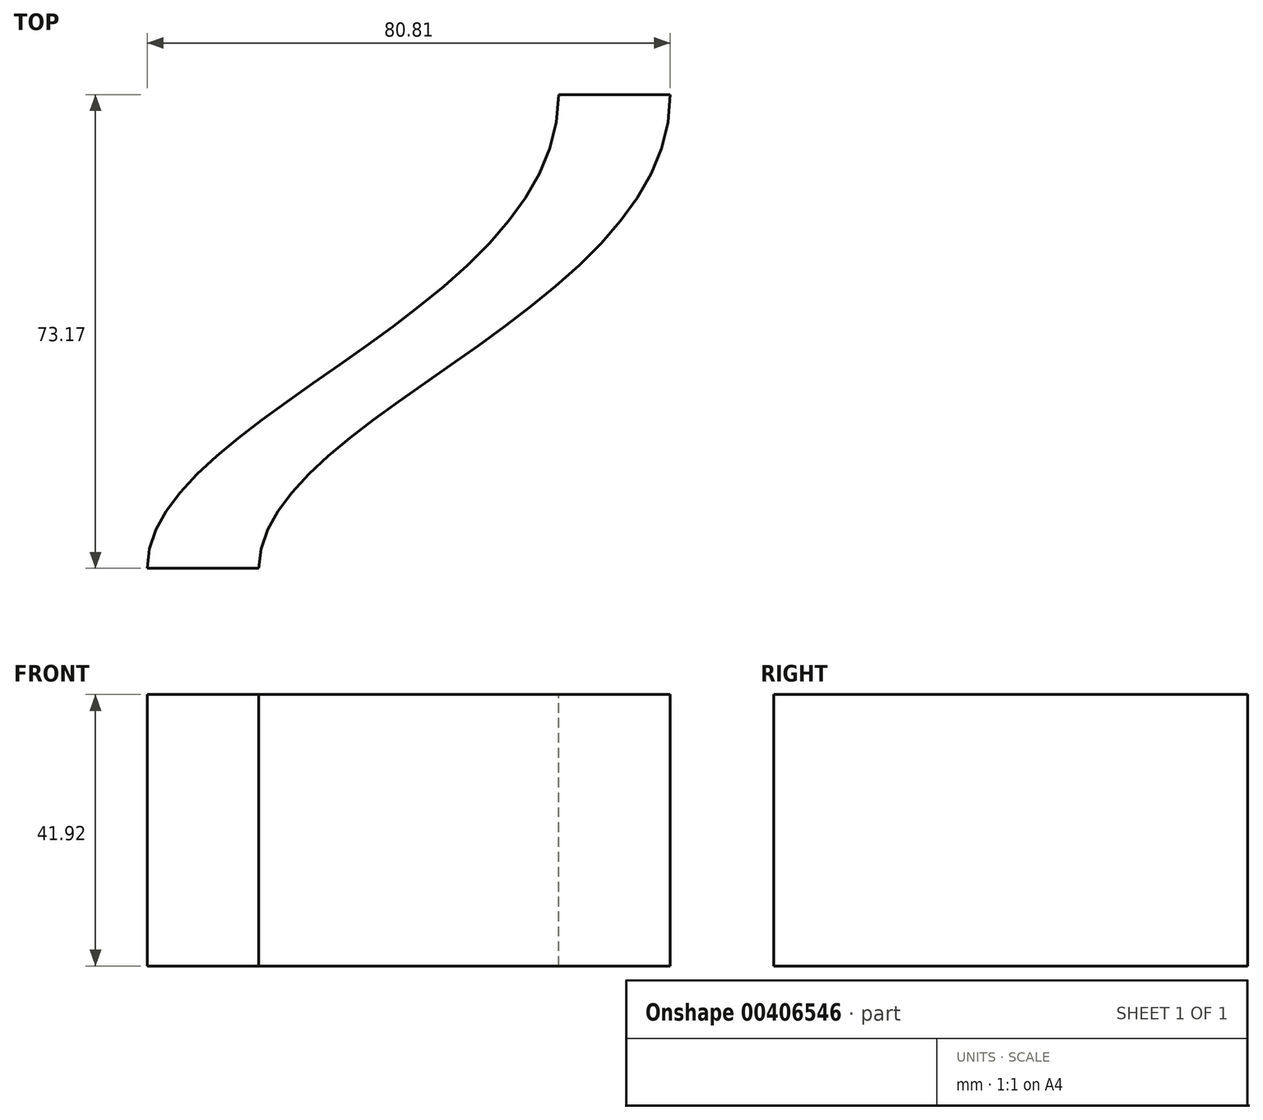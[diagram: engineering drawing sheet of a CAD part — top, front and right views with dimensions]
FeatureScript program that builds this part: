
annotation { "Feature Type Name" : "Feature", "Feature Type Description" : "" }
export const myFeature = defineFeature(function(context is Context, id is Id, definition is map)
    precondition{}
    {
        {
            var Q0;
            Q0=qCreatedBy(makeId("Front.planeOp"),FACE);
            var sketch = newSketch(context, id + "F0", { "sketchPlane" : qUnion([Q0])});
            skLineSegment(sketch, "E0", {"start": v(-49.03, 0) * mm, "end": v(-49.03, 41.92) * mm});
            skLineSegment(sketch, "E1", {"start": v(-49.03, 41.92) * mm, "end": v(-31.78, 41.92) * mm});
            skLineSegment(sketch, "E2", {"start": v(0, 0) * mm, "end": v(0, 115.46) * mm, "construction": true});
            skLineSegment(sketch, "E3", {"start": v(-31.78, 41.92) * mm, "end": v(-31.78, 0) * mm});
            skLineSegment(sketch, "E4", {"start": v(-31.78, 0) * mm, "end": v(-49.03, 0) * mm});
            skSolve(sketch);
        }
        {
            var Q0;
            Q0=qCreatedBy(makeId("Top.planeOp"),FACE);
            var sketch = newSketch(context, id + "F1", { "sketchPlane" : qUnion([Q0])});
            skFitSpline(sketch, "E5", {"points": [v(-31.78, 0) * mm, v(31.78, 73.17) * mm], "startDerivative": vector(0, 70.29) * mm, "endDerivative": vector(0, 99.51) * mm});
            skLineSegment(sketch, "E6", {"start": v(-31.78, 0) * mm, "end": v(-31.78, 36.7) * mm, "construction": true});
            skLineSegment(sketch, "E7", {"start": v(31.78, 0) * mm, "end": v(31.78, 73.17) * mm, "construction": true});
            skSolve(sketch);
        }
        {
            var Q0;
            Q0=makeQuery(id+"F0.imprint","IMPRINT",FACE,{"disambiguationData":[TD([[makeQuery(id+"F0.imprint","IMPRINT",EDGE,{"derivedFrom":sQuery(id+"F0.wireOp",EDGE,"E0")}),-1.0]])]});
            var Q1;
            Q1 = qSketchRegion(id + "F1", true);
            var Q2;
            Q2=sQuery(id+"F1.wireOp",EDGE,"E5");
            sweep(context, id + "F2", {"profiles" : qUnion([Q0, Q1]), "path" : qUnion([Q2]), "keepProfileOrientation" : true});
        }
    });
